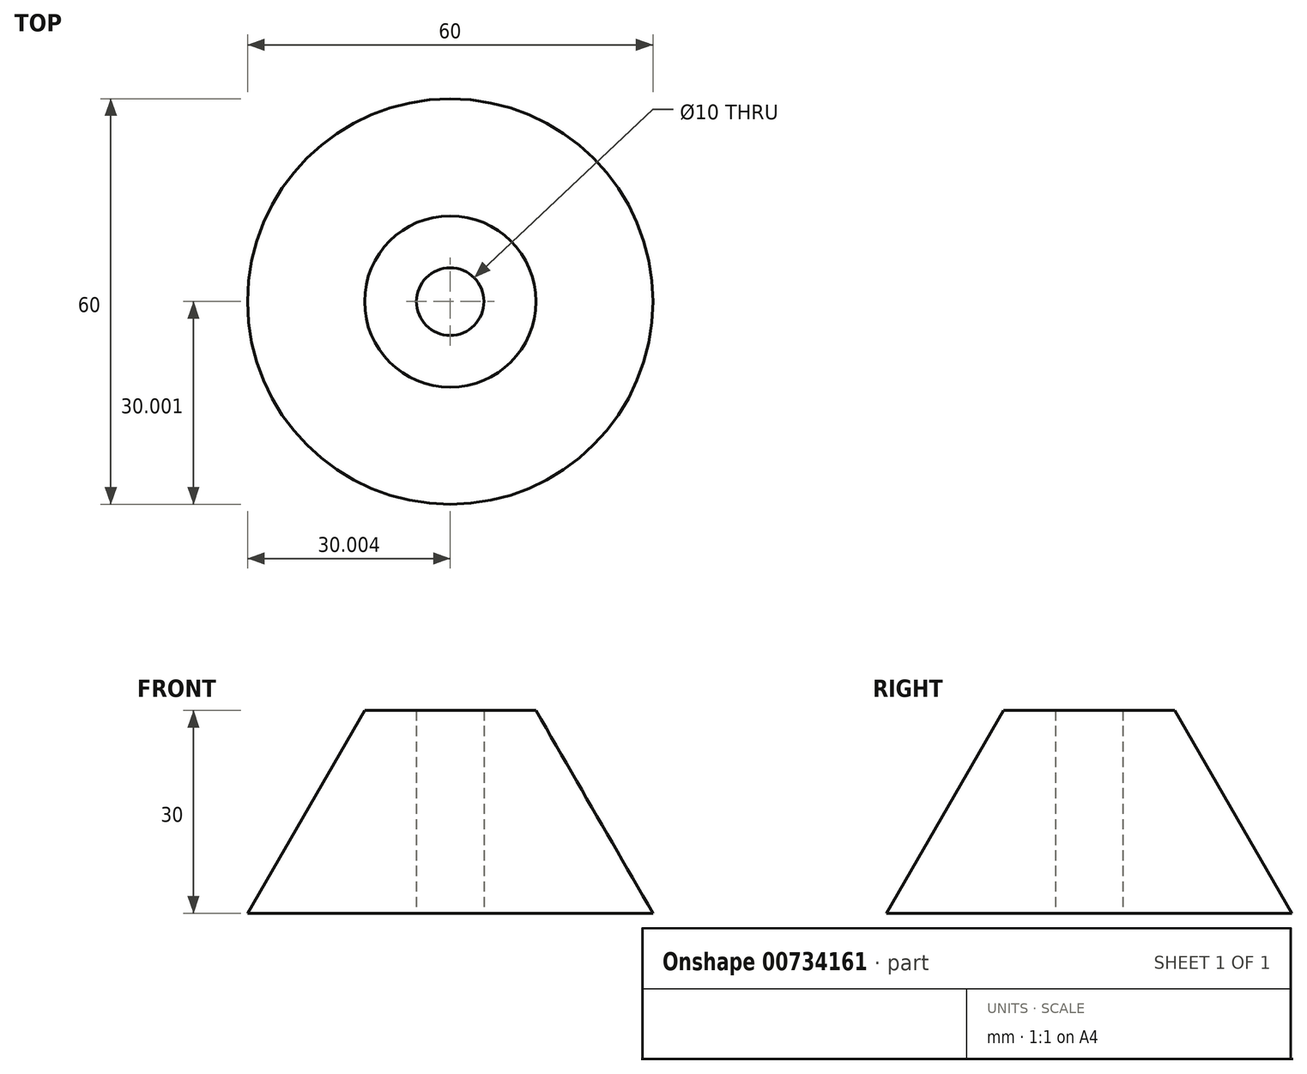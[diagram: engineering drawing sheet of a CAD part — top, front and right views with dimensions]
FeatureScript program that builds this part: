
annotation { "Feature Type Name" : "Feature", "Feature Type Description" : "" }
export const myFeature = defineFeature(function(context is Context, id is Id, definition is map)
    precondition{}
    {
        {
            var Q0;
            Q0=qCreatedBy(makeId("Top.planeOp"),FACE);
            var sketch = newSketch(context, id + "F0", { "sketchPlane" : qUnion([Q0])});
            skCircle(sketch, "E0", {"center": v(-26.04, 17.94) * mm, "radius": 30 * mm});
            skSolve(sketch);
        }
        {
            var Q0;
            Q0=makeQuery(id+"F0.imprint","IMPRINT",FACE,{"disambiguationData":[TD([[makeQuery(id+"F0.imprint","IMPRINT",EDGE,{"derivedFrom":sQuery(id+"F0.wireOp",EDGE,"E0")}),1.0]])]});
            var Q1;
            Q1=sQuery(id+"F0.wireOp",EDGE,"E0");
            extrude(context, id + "F1", {"entities" : qUnion([Q0]), "surfaceEntities" : qUnion([Q1]), "depth" : 30 * mm, "offsetDistance" : 25.4 * mm, "hasDraft" : true, "draftAngle" : 30 * degree, "draftPullDirection" : true});
        }
        {
            var Q0;
            Q0=sQuery(id+"F0.wireOp",VERTEX,"E0.center");
            var Q1;
            Q1=makeQuery(id+"F1.opExtrude","SWEPT_BODY",BODY,{"disambiguationData":[OSD([sQuery(id+"F0.wireOp",EDGE,"E0")])]});
            hole(context, id + "F2", {"style" : HoleStyle.SIMPLE, "endStyle" : HoleEndStyle.THROUGH, "oppositeDirection" : true, "holeDiameter" : 10 * mm, "majorDiameter" : 5 * mm, "isTappedThrough" : true, "tappedDepth" : 12 * mm, "tapClearance" : 3, "locations" : qUnion([Q0]), "scope" : qUnion([Q1])});
        }
    });
